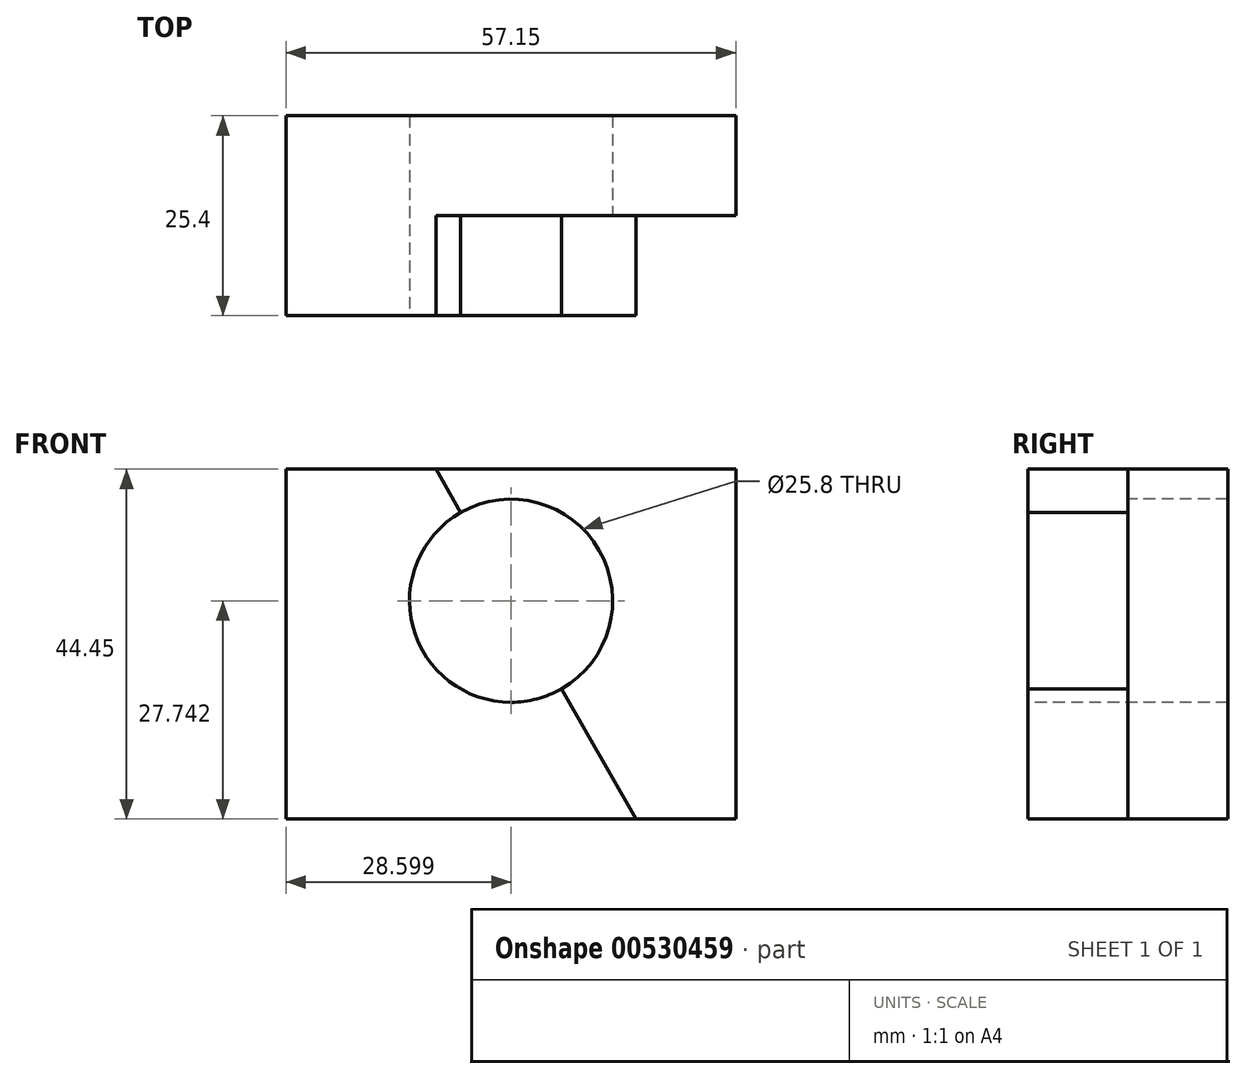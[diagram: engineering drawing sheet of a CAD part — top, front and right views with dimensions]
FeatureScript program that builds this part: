
annotation { "Feature Type Name" : "Feature", "Feature Type Description" : "" }
export const myFeature = defineFeature(function(context is Context, id is Id, definition is map)
    precondition{}
    {
        {
            var Q0;
            Q0=qCreatedBy(makeId("Front.planeOp"),FACE);
            var sketch = newSketch(context, id + "F0", { "sketchPlane" : qUnion([Q0])});
            skLineSegment(sketch, "E0", {"start": v(-58.83, 60.48) * mm, "end": v(-58.83, 16.03) * mm});
            skLineSegment(sketch, "E1", {"start": v(-58.83, 16.03) * mm, "end": v(-1.68, 16.03) * mm});
            skLineSegment(sketch, "E2", {"start": v(-1.68, 16.03) * mm, "end": v(-1.68, 60.48) * mm});
            skLineSegment(sketch, "E3", {"start": v(-1.68, 60.48) * mm, "end": v(-58.83, 60.48) * mm});
            skSolve(sketch);
        }
        {
            var Q0;
            Q0=makeQuery(id+"F0.imprint","IMPRINT",FACE,{"disambiguationData":[TD([[makeQuery(id+"F0.imprint","IMPRINT",EDGE,{"derivedFrom":sQuery(id+"F0.wireOp",EDGE,"E0")}),1.0]])]});
            extrude(context, id + "F1", {"entities" : qUnion([Q0]), "depth" : 25.4 * mm, "offsetDistance" : 25.4 * mm});
        }
        {
            var Q0;
            Q0=makeQuery(id+"F1.opExtrude","CAP_FACE",FACE,{"disambiguationData":[OSD([sQuery(id+"F0.wireOp",EDGE,"E0"),sQuery(id+"F0.wireOp",EDGE,"E1"),sQuery(id+"F0.wireOp",EDGE,"E2"),sQuery(id+"F0.wireOp",EDGE,"E3")])],"isStart":false});
            var sketch = newSketch(context, id + "F2", { "sketchPlane" : qUnion([Q0])});
            skLineSegment(sketch, "E4", {"start": v(-39.78, 60.48) * mm, "end": v(-14.38, 16.03) * mm});
            skCircle(sketch, "E5", {"center": v(-30.23, 43.77) * mm, "radius": 12.9 * mm});
            skSolve(sketch);
        }
        {
            var Q0;
            Q0 = qSketchRegion(id + "F2", true);
            var Q1;
            {var subQ0=makeQuery(id+"F1.opExtrude","CAP_EDGE",EDGE,{"disambiguationData":[OSD([sQuery(id+"F0.wireOp",EDGE,"E2")])],"isStart":false});Q1=makeQuery(id+"F2.imprint","IMPRINT",FACE,{"disambiguationData":[TD([[makeQuery(id+"F2.imprint","IMPRINT",EDGE,{"derivedFrom":subQ0}),1.0]])]});}
            extrude(context, id + "F3", {"entities" : qUnion([Q0, Q1]), "operationType" : NewBodyOperationType.REMOVE, "oppositeDirection" : true, "depth" : 12.7 * mm, "offsetDistance" : 25.4 * mm});
        }
        {
            var Q0;
            {var subQ0=sQuery(id+"F2.wireOp",EDGE,"E5");var subQ1=sQuery(id+"F2.wireOp",EDGE,"E4");var subQ2=makeQuery(id+"F2.imprint","INTERSECT",VERTEX,{"disambiguationData":[OD(0.0)],"derivedFrom":[subQ1,subQ0]});Q0=makeQuery(id+"F2.imprint","IMPRINT",FACE,{"disambiguationData":[TD([[makeQuery(id+"F2.imprint","IMPRINT",EDGE,{"disambiguationData":[TD([[subQ2,-1.0]])],"derivedFrom":subQ1}),1.0]])]});}
            var Q1;
            {var subQ0=sQuery(id+"F2.wireOp",EDGE,"E5");var subQ1=sQuery(id+"F2.wireOp",EDGE,"E4");var subQ2=makeQuery(id+"F2.imprint","INTERSECT",VERTEX,{"disambiguationData":[OD(0.0)],"derivedFrom":[subQ1,subQ0]});Q1=makeQuery(id+"F2.imprint","IMPRINT",FACE,{"disambiguationData":[TD([[makeQuery(id+"F2.imprint","IMPRINT",EDGE,{"disambiguationData":[TD([[subQ2,-1.0]])],"derivedFrom":subQ1}),-1.0]])]});}
            extrude(context, id + "F4", {"entities" : qUnion([Q0, Q1]), "operationType" : NewBodyOperationType.REMOVE, "oppositeDirection" : true, "depth" : 25.4 * mm, "offsetDistance" : 25.4 * mm});
        }
    });
